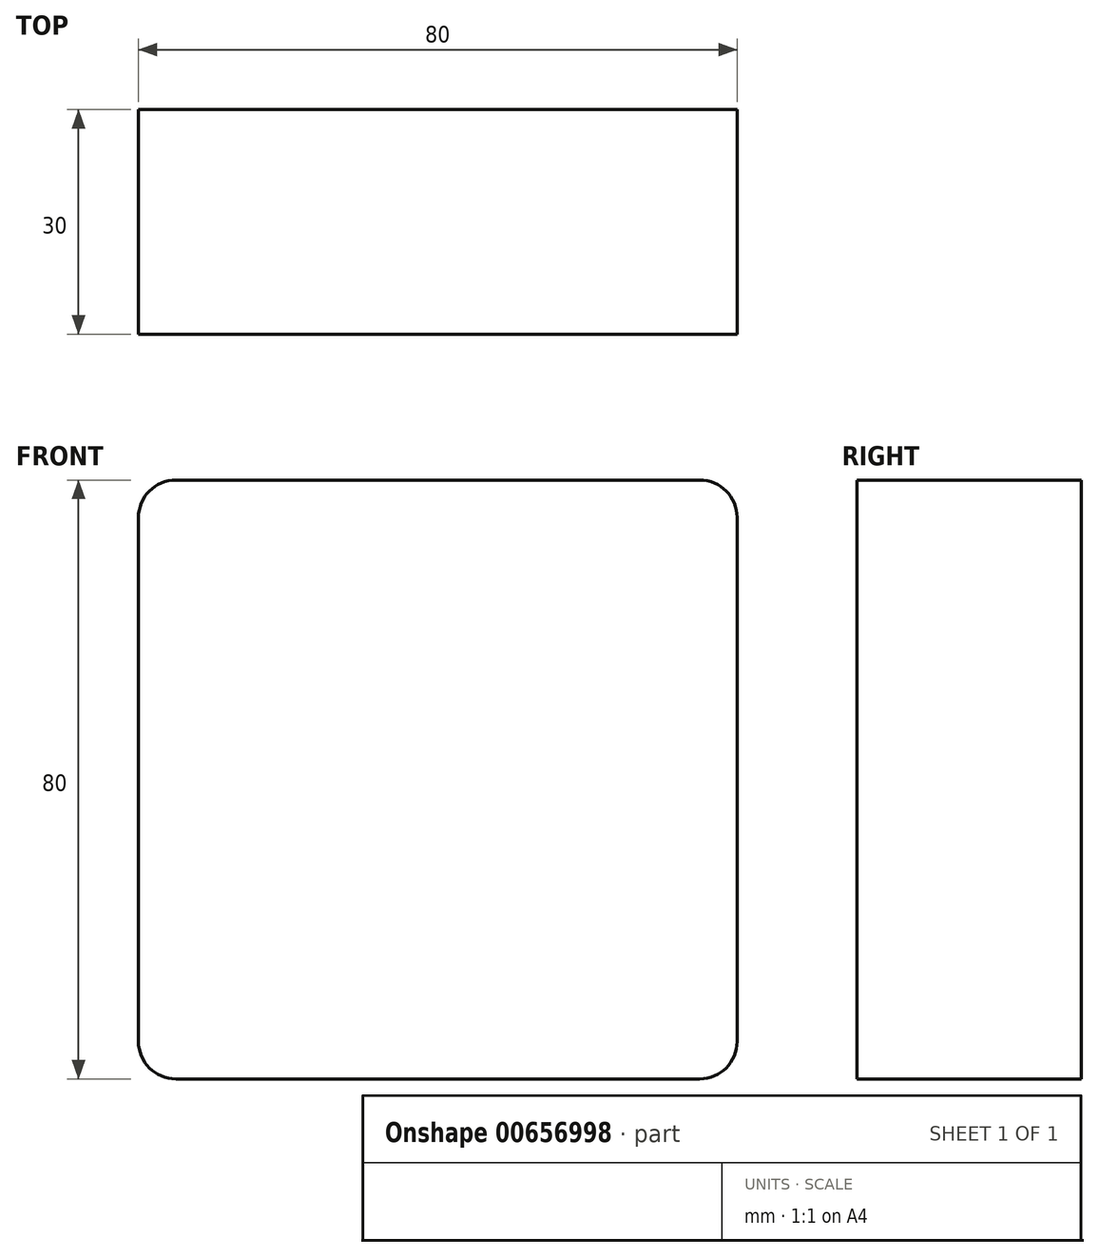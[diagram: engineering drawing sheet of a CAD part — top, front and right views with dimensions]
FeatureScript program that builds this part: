
annotation { "Feature Type Name" : "Feature", "Feature Type Description" : "" }
export const myFeature = defineFeature(function(context is Context, id is Id, definition is map)
    precondition{}
    {
        {
            var Q0;
            Q0=qCreatedBy(makeId("Front.planeOp"),FACE);
            var sketch = newSketch(context, id + "F0", { "sketchPlane" : qUnion([Q0])});
            skLineSegment(sketch, "E0.bottom", {"start": v(-80, 62.5) * mm, "end": v(0, 62.5) * mm});
            skLineSegment(sketch, "E0.top", {"start": v(-80, -17.5) * mm, "end": v(0, -17.5) * mm});
            skLineSegment(sketch, "E0.left", {"start": v(-80, 62.5) * mm, "end": v(-80, -17.5) * mm});
            skLineSegment(sketch, "E0.right", {"start": v(0, 62.5) * mm, "end": v(0, -17.5) * mm});
            skSolve(sketch);
        }
        {
            var Q0;
            Q0=makeQuery(id+"F0.imprint","IMPRINT",FACE,{"disambiguationData":[TD([[makeQuery(id+"F0.imprint","IMPRINT",EDGE,{"derivedFrom":sQuery(id+"F0.wireOp",EDGE,"E0.bottom")}),-1.0]])]});
            extrude(context, id + "F1", {"entities" : qUnion([Q0]), "depth" : 30 * mm, "offsetDistance" : 25.4 * mm});
        }
        {
            var Q0;
            Q0=makeQuery(id+"F1.opExtrude","SWEPT_EDGE",EDGE,{"disambiguationData":[OSD([sQuery(id+"F0.wireOp",EDGE,"E0.bottom"),sQuery(id+"F0.wireOp",EDGE,"E0.left")])]});
            var Q1;
            Q1=makeQuery(id+"F1.opExtrude","SWEPT_EDGE",EDGE,{"disambiguationData":[OSD([sQuery(id+"F0.wireOp",EDGE,"E0.bottom"),sQuery(id+"F0.wireOp",EDGE,"E0.right")])]});
            var Q2;
            Q2=makeQuery(id+"F1.opExtrude","SWEPT_EDGE",EDGE,{"disambiguationData":[OSD([sQuery(id+"F0.wireOp",EDGE,"E0.top"),sQuery(id+"F0.wireOp",EDGE,"E0.right")])]});
            var Q3;
            Q3=makeQuery(id+"F1.opExtrude","SWEPT_EDGE",EDGE,{"disambiguationData":[OSD([sQuery(id+"F0.wireOp",EDGE,"E0.top"),sQuery(id+"F0.wireOp",EDGE,"E0.left")])]});
            fillet(context, id + "F2", {"entities" : qUnion([Q0, Q1, Q2, Q3]), "radius" : 5 * mm, "tangentPropagation" : true, "allowEdgeOverflow" : false});
        }
    });
